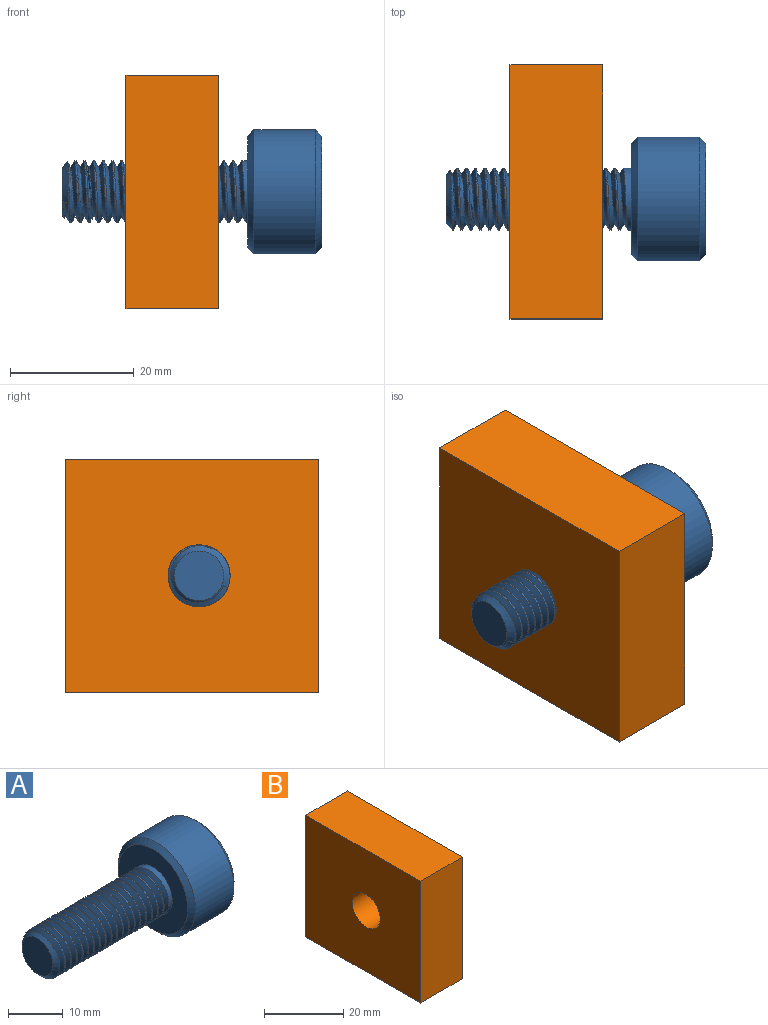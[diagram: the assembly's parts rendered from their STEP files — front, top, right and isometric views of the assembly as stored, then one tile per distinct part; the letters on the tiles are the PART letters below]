
ASSEMBLY  parts=2 mates=1
PART A: 20 faces, bbox 43.3x21.1x21.1 mm
  f0: cylinder r=5mm len=29mm, axis (1,0,0), area 167.6mm2, adj f3,f15,f17,f18,f19
  f1: cone r=5mm half-angle=45deg, axis (1,0,0), area 35.3mm2, adj f4,f7,f8,f9,f10,f11,f12
  f2: cylinder r=10mm len=20mm, axis (1,0,0), area 628.3mm2, adj f5,f6
  f3: plane 18x18mm, normal (-1,0,0), area 175.9mm2, adj f0,f5
  f4: plane 18x18mm, normal (1,0,0), area 141.4mm2, adj f1,f6
  f5: cone r=10mm half-angle=45deg, axis (1,0,0), area 84.4mm2, adj f2,f3
  f6: cone r=9mm half-angle=45deg, axis (-1,0,0), area 84.4mm2, adj f2,f4
  f7: plane 9.79x5.51mm, normal (0,-0.95,-0.3), area 53.7mm2, adj f1,f8,f12,f13
  f8: plane 9.79x5.65mm, normal (0,-0.21,-0.98), area 53.7mm2, adj f1,f7,f9,f13
  f9: plane 9.79x4.28mm, normal (0,0.74,-0.67), area 53.7mm2, adj f1,f8,f10,f13
  f10: plane 9.79x5.51mm, normal (0,0.95,0.3), area 53.7mm2, adj f1,f9,f11,f13
  f11: plane 10.86x6.72mm, normal (0,0.21,0.98), area 53.7mm2, adj f1,f10,f12,f13
  f12: plane 9.79x4.28mm, normal (0,-0.74,0.67), area 53.7mm2, adj f1,f7,f11,f13
  f13: plane 11.3x11.03mm, normal (1,0,0), area 87mm2, adj f7,f8,f9,f10,f11,f12
  f14: plane 8x8mm, normal (-1,0,0), area 50.3mm2, adj f15
  f15: cone r=4mm half-angle=45deg, axis (1,0,0), area 26.1mm2, adj f0,f14,f16,f19
  f16: plane 1.08x0.79mm, normal (0,1,0), area 0.2mm2, adj f15,f18,f19
  f17: plane 1.25x0.94mm, normal (0,0.5,-0.87), area 0.7mm2, adj f0,f18,f19
  f18: bspline ~29.63x11.55mm, area 675.8mm2, adj f0,f16,f17,f19
  f19: bspline ~29.63x11.55mm, area 665.3mm2, adj f0,f15,f16,f17,f18
PART B: 7 faces, bbox 15x41x37.7 mm
  f0: plane 37.7x15mm, normal (0,-1,0), area 565.5mm2, adj f1,f4,f5,f6
  f1: plane 41x15mm, normal (0,0,-1), area 615.1mm2, adj f0,f2,f5,f6
  f2: plane 37.7x15mm, normal (0,1,0), area 565.5mm2, adj f1,f4,f5,f6
  f3: cylinder r=5mm len=15mm, axis (1,0,0), area 471.2mm2, adj f5,f6
  f4: plane 41x15mm, normal (0,0,1), area 615.1mm2, adj f0,f2,f5,f6
  f5: plane 41x37.7mm, normal (-1,0,0), area 1467.3mm2, adj f0,f1,f2,f3,f4
  f6: plane 41x37.7mm, normal (1,0,0), area 1467.3mm2, adj f0,f1,f2,f3,f4
PLACE A rot(axis=(-1,0,0),67.2deg) t=(45.49,3.67,-11.67)mm
PLACE B t=(28.82,3.67,-11.67)mm fixed
MATE cylindrical B.f3 <-> A.f0  axis (1,0,0) through (28.82,3.67,-11.67)mm
